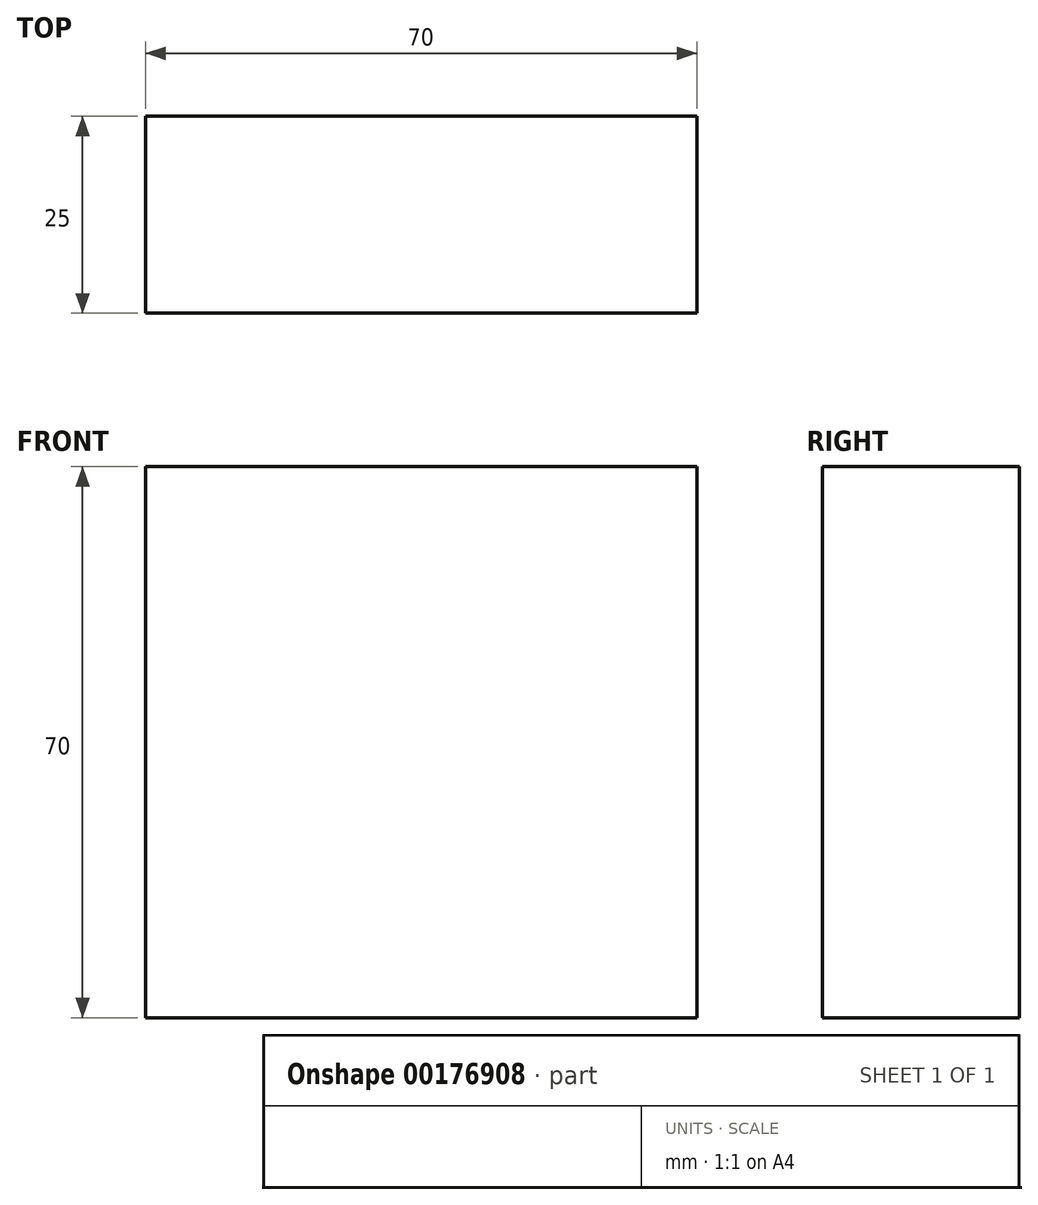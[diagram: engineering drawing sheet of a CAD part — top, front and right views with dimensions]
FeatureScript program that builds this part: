
annotation { "Feature Type Name" : "Feature", "Feature Type Description" : "" }
export const myFeature = defineFeature(function(context is Context, id is Id, definition is map)
    precondition{}
    {
        {
            var Q0;
            Q0=qCreatedBy(makeId("Front.planeOp"),FACE);
            var sketch = newSketch(context, id + "F0", { "sketchPlane" : qUnion([Q0])});
            skLineSegment(sketch, "E0.bottom", {"start": v(30, 30) * mm, "end": v(-40, 30) * mm});
            skLineSegment(sketch, "E0.top", {"start": v(30, -40) * mm, "end": v(-40, -40) * mm});
            skLineSegment(sketch, "E0.left", {"start": v(30, 30) * mm, "end": v(30, -40) * mm});
            skLineSegment(sketch, "E0.right", {"start": v(-40, 30) * mm, "end": v(-40, -40) * mm});
            skSolve(sketch);
        }
        {
            var Q0;
            Q0 = qSketchRegion(id + "F0", true);
            extrude(context, id + "F1", {"entities" : qUnion([Q0]), "depth" : 25 * mm});
        }
    });
